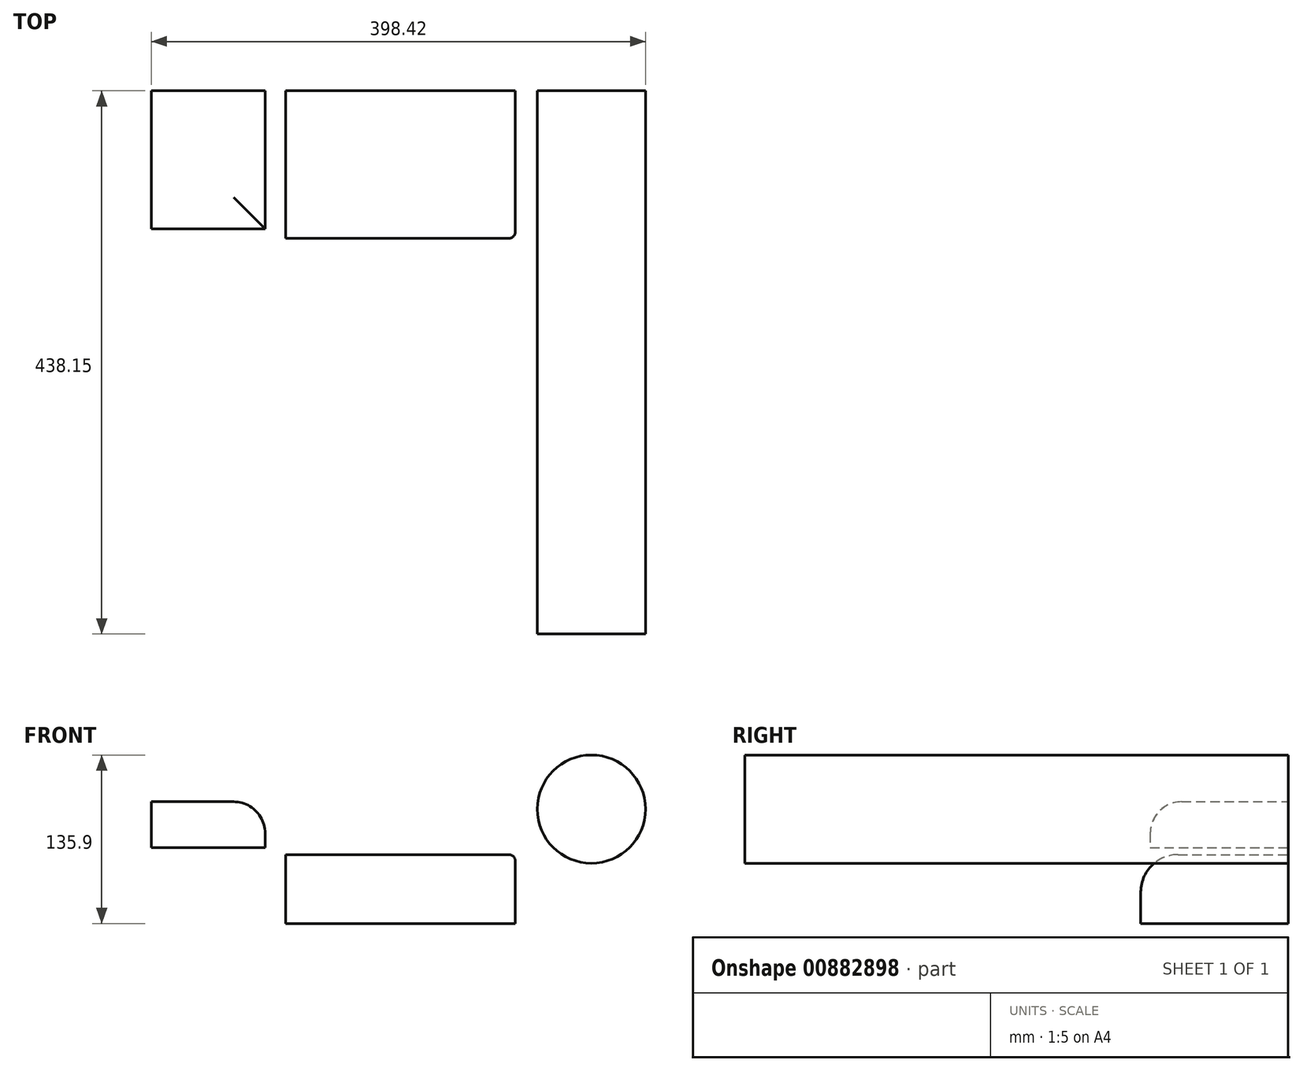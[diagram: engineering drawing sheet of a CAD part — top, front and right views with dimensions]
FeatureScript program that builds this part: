
annotation { "Feature Type Name" : "Feature", "Feature Type Description" : "" }
export const myFeature = defineFeature(function(context is Context, id is Id, definition is map)
    precondition{}
    {
        {
            var Q0;
            Q0=qCreatedBy(makeId("Front.planeOp"),FACE);
            var sketch = newSketch(context, id + "F0", { "sketchPlane" : qUnion([Q0])});
            skLineSegment(sketch, "E0.bottom", {"start": v(-58.8, 44.1) * mm, "end": v(126.25, 44.1) * mm});
            skLineSegment(sketch, "E0.top", {"start": v(-58.8, -11.46) * mm, "end": v(126.25, -11.46) * mm});
            skLineSegment(sketch, "E0.left", {"start": v(-58.8, 44.1) * mm, "end": v(-58.8, -11.46) * mm});
            skLineSegment(sketch, "E0.right", {"start": v(126.25, 44.1) * mm, "end": v(126.25, -11.46) * mm});
            skSolve(sketch);
        }
        {
            var Q0;
            Q0=makeQuery(id+"F0.imprint","IMPRINT",FACE,{"disambiguationData":[TD([[makeQuery(id+"F0.imprint","IMPRINT",EDGE,{"derivedFrom":sQuery(id+"F0.wireOp",EDGE,"E0.bottom")}),-1.0]])]});
            extrude(context, id + "F1", {"entities" : qUnion([Q0]), "depth" : 118.87 * mm, "offsetDistance" : 25.4 * mm});
        }
        {
            var Q0;
            Q0=makeQuery(id+"F1.opExtrude","CAP_EDGE",EDGE,{"disambiguationData":[OSD([sQuery(id+"F0.wireOp",EDGE,"E0.bottom")])],"isStart":false});
            fillet(context, id + "F2", {"entities" : qUnion([Q0]), "radius" : 30.05 * mm, "tangentPropagation" : true, "allowEdgeOverflow" : false});
        }
        {
            var Q0;
            Q0=makeQuery(id+"F1.opExtrude","SWEPT_EDGE",EDGE,{"disambiguationData":[OSD([sQuery(id+"F0.wireOp",EDGE,"E0.bottom"),sQuery(id+"F0.wireOp",EDGE,"E0.right")])]});
            fillet(context, id + "F3", {"entities" : qUnion([Q0]), "radius" : 5.08 * mm, "tangentPropagation" : true, "allowEdgeOverflow" : false});
        }
        {
            var Q0;
            Q0=qCreatedBy(makeId("Front.planeOp"),FACE);
            var sketch = newSketch(context, id + "F4", { "sketchPlane" : qUnion([Q0])});
            skLineSegment(sketch, "E1.bottom", {"start": v(-167.16, 86.73) * mm, "end": v(-75.47, 86.73) * mm});
            skLineSegment(sketch, "E1.top", {"start": v(-167.16, 49.64) * mm, "end": v(-75.47, 49.64) * mm});
            skLineSegment(sketch, "E1.left", {"start": v(-167.16, 86.73) * mm, "end": v(-167.16, 49.64) * mm});
            skLineSegment(sketch, "E1.right", {"start": v(-75.47, 86.73) * mm, "end": v(-75.47, 49.64) * mm});
            skSolve(sketch);
        }
        {
            var Q0;
            Q0=makeQuery(id+"F4.imprint","IMPRINT",FACE,{"disambiguationData":[TD([[makeQuery(id+"F4.imprint","IMPRINT",EDGE,{"derivedFrom":sQuery(id+"F4.wireOp",EDGE,"E1.bottom")}),-1.0]])]});
            extrude(context, id + "F5", {"entities" : qUnion([Q0]), "depth" : 111.25 * mm, "offsetDistance" : 25.4 * mm});
        }
        {
            var Q0;
            Q0=qCreatedBy(makeId("Front.planeOp"),FACE);
            var sketch = newSketch(context, id + "F6", { "sketchPlane" : qUnion([Q0])});
            skCircle(sketch, "E2", {"center": v(187.61, 80.78) * mm, "radius": 43.65 * mm});
            skSolve(sketch);
        }
        {
            var Q0;
            Q0 = qSketchRegion(id + "F6", true);
            extrude(context, id + "F7", {"entities" : qUnion([Q0]), "depth" : 438.15 * mm, "offsetDistance" : 25.4 * mm});
        }
        {
            var Q0;
            Q0=makeQuery(id+"F5.opExtrude","SWEPT_EDGE",EDGE,{"disambiguationData":[OSD([sQuery(id+"F4.wireOp",EDGE,"E1.bottom"),sQuery(id+"F4.wireOp",EDGE,"E1.right")])]});
            var Q1;
            Q1=makeQuery(id+"F5.opExtrude","CAP_EDGE",EDGE,{"disambiguationData":[OSD([sQuery(id+"F4.wireOp",EDGE,"E1.bottom")])],"isStart":false});
            fillet(context, id + "F8", {"entities" : qUnion([Q0, Q1]), "radius" : 25.4 * mm, "tangentPropagation" : true, "allowEdgeOverflow" : false});
        }
    });
